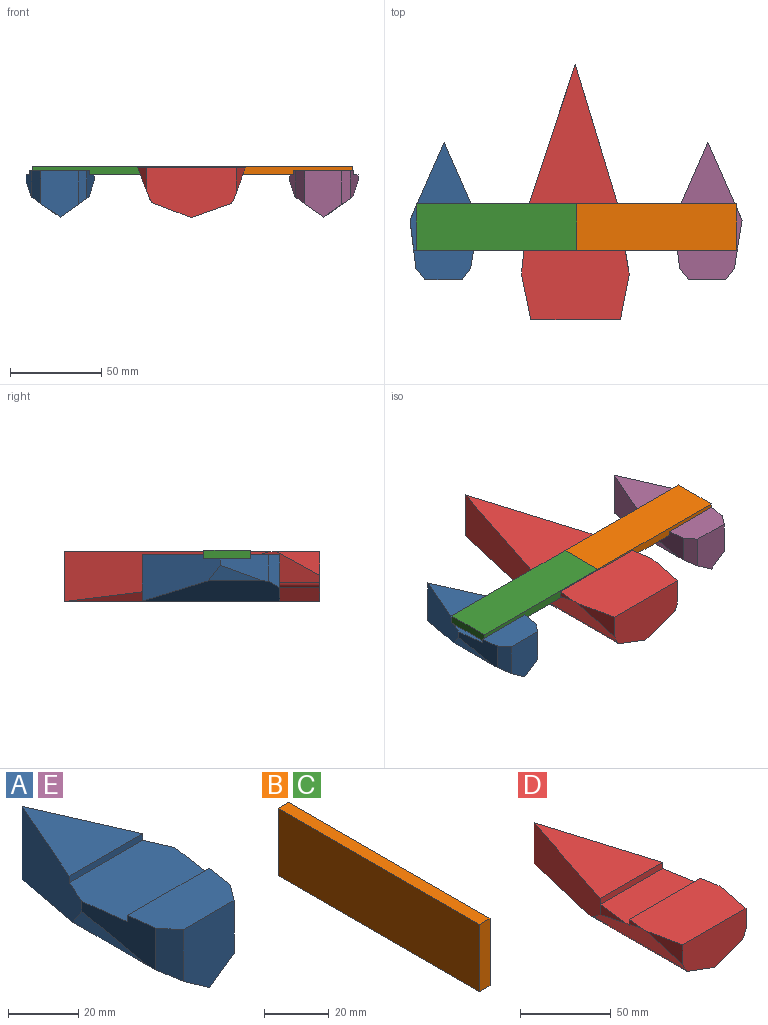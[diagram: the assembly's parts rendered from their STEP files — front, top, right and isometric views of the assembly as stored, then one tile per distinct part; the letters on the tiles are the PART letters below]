
ASSEMBLY  parts=5 mates=4
PART A: 16 faces, bbox 37.4x75.4x25.4 mm
  f0: plane 42.77x25.4mm, normal (0.92,0.4,0), area 831.5mm2, adj f1,f6,f7,f9,f10,f13,f15
  f1: plane 33.76x29.54mm, normal (0,0,1), area 498.7mm2, adj f0,f7,f13
  f2: plane 32.83x16.2mm, normal (0,0,1), area 471mm2, adj f3,f4,f5,f6,f8,f14
  f3: plane 26.5x14.51mm, normal (-0.99,-0.12,0), area 243.5mm2, adj f2,f7,f8,f11,f12,f14,f15
  f4: plane 25.4x20.42mm, normal (0,-1,0), area 445.2mm2, adj f2,f5,f8,f9,f12
  f5: plane 18.44x6.08mm, normal (0.8,-0.61,0), area 128.5mm2, adj f2,f4,f6,f9
  f6: plane 26.5x15.17mm, normal (0.99,-0.16,0), area 267.2mm2, adj f0,f2,f5,f9,f10,f14,f15
  f7: plane 42.77x25.4mm, normal (-0.92,0.4,0), area 832.7mm2, adj f0,f1,f3,f11,f12,f13,f15
  f8: plane 17.99x6.08mm, normal (-0.78,-0.63,0), area 127.2mm2, adj f2,f3,f4,f12
  f9: plane 75.35x15.88mm, normal (0.58,0,-0.82), area 1076.6mm2, adj f0,f4,f5,f6,f10,f12
  f10: plane 24.49x8.85mm, normal (0.95,0,-0.31), area 113.8mm2, adj f0,f6,f9
  f11: plane 29.68x8.48mm, normal (-0.95,0,-0.32), area 132.8mm2, adj f3,f7,f12
  f12: plane 75.35x15.87mm, normal (-0.58,0,-0.82), area 1088.3mm2, adj f3,f4,f7,f8,f9,f11
  f13: plane 29.54x2.29mm, normal (0,-1,0), area 67.5mm2, adj f0,f1,f7,f15
  f14: plane 32.83x2.29mm, normal (0,1,0), area 75mm2, adj f2,f3,f6,f15
  f15: plane 37.43x25.4mm, normal (0,0,1), area 877.5mm2, adj f0,f3,f6,f7,f13,f14
PART B: 6 faces, bbox 4.7x88x25.4 mm
  f0: plane 87.98x25.4mm, normal (1,0,0), area 2234.6mm2, adj f1,f3,f4,f5
  f1: plane 25.4x4.69mm, normal (0,1,0), area 119.2mm2, adj f0,f2,f4,f5
  f2: plane 87.98x25.4mm, normal (-1,0,0), area 2234.6mm2, adj f1,f3,f4,f5
  f3: plane 25.4x4.69mm, normal (0,-1,0), area 119.2mm2, adj f0,f2,f4,f5
  f4: plane 87.98x4.69mm, normal (0,0,1), area 412.9mm2, adj f0,f1,f2,f3
  f5: plane 87.98x4.69mm, normal (0,0,-1), area 412.9mm2, adj f0,f1,f2,f3
PART C: same geometry as B
PART D: 19 faces, bbox 58.9x140x27.4 mm
  f0: plane 76.55x48.35mm, normal (0,0,1), area 1850.6mm2, adj f6,f7,f18
  f1: plane 22.65x6.83mm, normal (-0.99,0.11,0), area 77.9mm2, adj f7,f13,f17
  f2: plane 10.72x3.23mm, normal (-0.99,0.11,0), area 17.5mm2, adj f5,f13,f16
  f3: plane 49.14x27.43mm, normal (0,-1,0), area 1114.1mm2, adj f4,f5,f8,f10,f11,f12,f13,f14
  f4: plane 23.69x13.07mm, normal (-0.98,-0.2,0), area 158.2mm2, adj f3,f5,f13
  f5: plane 58.9x38.06mm, normal (0,0,1), area 2102.3mm2, adj f2,f3,f4,f8,f9,f13,f16
  f6: plane 76.55x27.43mm, normal (0.96,0.29,0), area 1860.4mm2, adj f0,f7,f9,f11,f12,f18
  f7: plane 76.55x27.43mm, normal (-0.95,0.31,0), area 1790.1mm2, adj f0,f1,f6,f13,f14,f15,f18
  f8: plane 24.98x13.61mm, normal (0.98,-0.19,0), area 174.1mm2, adj f3,f5,f9,f10
  f9: plane 38.48x17.93mm, normal (0.99,0.16,0), area 250.5mm2, adj f5,f6,f8,f10,f11,f16,f17
  f10: plane 61.41x17.09mm, normal (0.94,0,-0.34), area 604.3mm2, adj f3,f8,f9,f11
  f11: cylinder r=5.11mm len=69.29mm, axis (0,-1,0), area 223.3mm2, adj f3,f6,f9,f10,f12
  f12: plane 140.01x21.4mm, normal (0.34,0,-0.94), area 2378.1mm2, adj f3,f6,f11,f15
  f13: plane 70.68x17.17mm, normal (-0.94,0,-0.35), area 812.1mm2, adj f1,f2,f3,f4,f5,f7,f14,f16
  f14: cylinder r=4.51mm len=78.64mm, axis (0,-1,0), area 282.9mm2, adj f3,f7,f13,f15
  f15: plane 140.01x20.19mm, normal (-0.35,0,-0.94), area 2360.3mm2, adj f3,f7,f12,f14
  f16: plane 55.49x4.06mm, normal (0,1,0), area 225.4mm2, adj f2,f5,f9,f13,f17
  f17: plane 55.18x25.4mm, normal (0,0,1), area 1318.4mm2, adj f1,f9,f13,f16,f18
  f18: plane 48.35x4.06mm, normal (0,-1,0), area 196.5mm2, adj f0,f6,f7,f17
PART E: same geometry as A
PLACE A rot(axis=(1,0,0),0deg) t=(-89.85,-18.78,-3.03)mm
PLACE B rot(axis=(0.58,-0.58,0.58),120deg) t=(30.61,-9.85,24.78)mm
PLACE C rot(axis=(0.58,0.58,-0.58),120deg) t=(-65.01,-9.85,20.09)mm
PLACE D t=(-17.92,-9.85,-3.28)mm fixed
PLACE E t=(54.82,-18.78,-3.03)mm
MATE fastened C.f1 <-> B.f1  axis (1,0,0) through (-17.2,-22.55,22.43)mm
MATE fastened E.f15 <-> B.f2  axis (0,0,1) through (54.73,-22.55,20.09)mm
MATE fastened D.f17 <-> B.f2  axis (0,0,1) through (-18.93,-9.85,20.09)mm
MATE fastened A.f15 <-> C.f0  axis (0,0,1) through (-89.94,-22.55,20.09)mm
